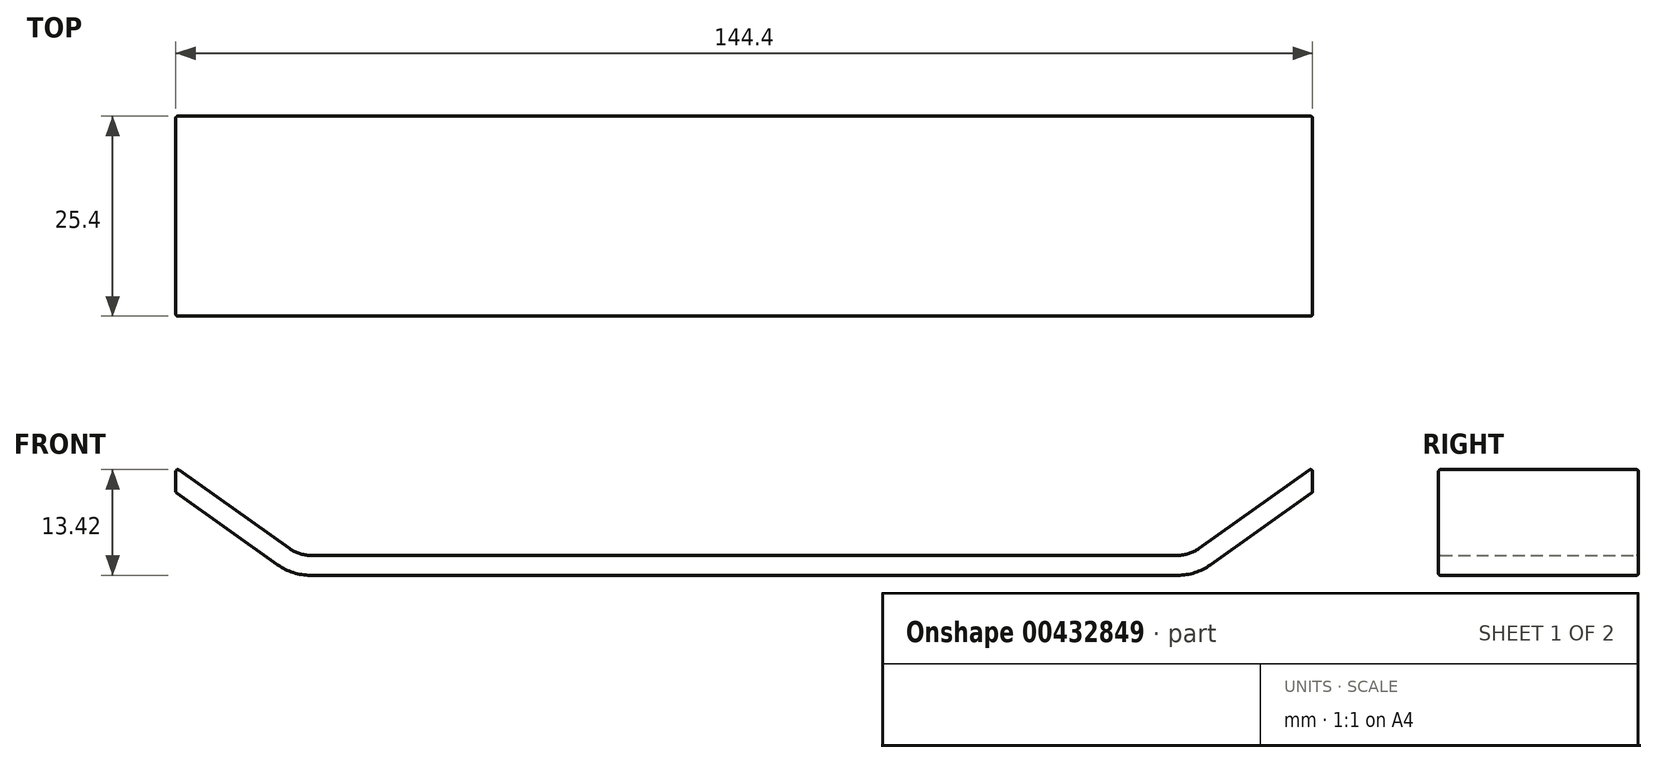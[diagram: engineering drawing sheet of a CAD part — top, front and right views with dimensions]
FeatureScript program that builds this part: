
annotation { "Feature Type Name" : "Feature", "Feature Type Description" : "" }
export const myFeature = defineFeature(function(context is Context, id is Id, definition is map)
    precondition{}
    {
        {
            var Q0;
            Q0=qCreatedBy(makeId("Front.planeOp"),FACE);
            var sketch = newSketch(context, id + "F0", { "sketchPlane" : qUnion([Q0])});
            skLineSegment(sketch, "E0", {"start": v(0, 0) * mm, "end": v(-55.08, 0) * mm});
            skArc(sketch, "E1", {"start": v(-59.23, 1.33) * mm, "mid": v(-57.26, 0.34) * mm, "end": v(-55.08, 0) * mm});
            skLineSegment(sketch, "E2", {"start": v(-59.23, 1.33) * mm, "end": v(-72.2, 10.54) * mm});
            skLineSegment(sketch, "E3.0", {"start": v(-57.76, 3.4) * mm, "end": v(-72.2, 13.66) * mm});
            skArc(sketch, "E3.1", {"start": v(-57.76, 3.4) * mm, "mid": v(-56.49, 2.76) * mm, "end": v(-55.08, 2.54) * mm});
            skLineSegment(sketch, "E3.2", {"start": v(0, 2.54) * mm, "end": v(-55.08, 2.54) * mm});
            skLineSegment(sketch, "E4", {"start": v(-72.2, 13.66) * mm, "end": v(-72.2, 10.54) * mm});
            skLineSegment(sketch, "E5.MirrorCS", {"start": v(72.2, 13.66) * mm, "end": v(72.2, 10.54) * mm});
            skArc(sketch, "E6.MirrorCS", {"start": v(57.76, 3.4) * mm, "mid": v(56.49, 2.76) * mm, "end": v(55.08, 2.54) * mm});
            skArc(sketch, "E7.MirrorCS", {"start": v(59.23, 1.33) * mm, "mid": v(57.26, 0.34) * mm, "end": v(55.08, 0) * mm});
            skLineSegment(sketch, "E8.MirrorCS", {"start": v(59.23, 1.33) * mm, "end": v(72.2, 10.54) * mm});
            skLineSegment(sketch, "E9.MirrorCS", {"start": v(0, 2.54) * mm, "end": v(55.08, 2.54) * mm});
            skLineSegment(sketch, "E10.MirrorCS", {"start": v(57.76, 3.4) * mm, "end": v(72.2, 13.66) * mm});
            skLineSegment(sketch, "E11.MirrorCS", {"start": v(0, 0) * mm, "end": v(55.08, 0) * mm});
            skSolve(sketch);
        }
        {
            var Q0;
            Q0=makeQuery(id+"F0.imprint","IMPRINT",FACE,{"disambiguationData":[TD([[makeQuery(id+"F0.imprint","IMPRINT",EDGE,{"derivedFrom":sQuery(id+"F0.wireOp",EDGE,"E0")}),-1.0]])]});
            extrude(context, id + "F1", {"entities" : qUnion([Q0]), "depth" : 25.4 * mm});
        }
        {
            var Q0;
            Q0=makeQuery(id+"F1.opExtrude","CAP_FACE",FACE,{"disambiguationData":[OSD([sQuery(id+"F0.wireOp",EDGE,"E0"),sQuery(id+"F0.wireOp",EDGE,"E1"),sQuery(id+"F0.wireOp",EDGE,"E2"),sQuery(id+"F0.wireOp",EDGE,"E3.0"),sQuery(id+"F0.wireOp",EDGE,"E3.1"),sQuery(id+"F0.wireOp",EDGE,"E3.2"),sQuery(id+"F0.wireOp",EDGE,"E4"),sQuery(id+"F0.wireOp",EDGE,"E5.MirrorCS"),sQuery(id+"F0.wireOp",EDGE,"E6.MirrorCS"),sQuery(id+"F0.wireOp",EDGE,"E7.MirrorCS"),sQuery(id+"F0.wireOp",EDGE,"E8.MirrorCS"),sQuery(id+"F0.wireOp",EDGE,"E9.MirrorCS"),sQuery(id+"F0.wireOp",EDGE,"E10.MirrorCS"),sQuery(id+"F0.wireOp",EDGE,"E11.MirrorCS")])],"isStart":true});
            var Q1;
            Q1=makeQuery(id+"F1.opExtrude","CAP_EDGE",EDGE,{"disambiguationData":[OSD([sQuery(id+"F0.wireOp",EDGE,"E3.0")])],"isStart":false});
            var Q2;
            Q2=makeQuery(id+"F1.opExtrude","CAP_EDGE",EDGE,{"disambiguationData":[OSD([sQuery(id+"F0.wireOp",EDGE,"E3.0")])],"isStart":true});
            var Q3;
            Q3=makeQuery(id+"F1.opExtrude","CAP_EDGE",EDGE,{"disambiguationData":[OSD([sQuery(id+"F0.wireOp",EDGE,"E3.2"),sQuery(id+"F0.wireOp",EDGE,"E9.MirrorCS")])],"isStart":false});
            var Q4;
            Q4=makeQuery(id+"F1.opExtrude","CAP_EDGE",EDGE,{"disambiguationData":[OSD([sQuery(id+"F0.wireOp",EDGE,"E2")])],"isStart":true});
            var Q5;
            Q5=makeQuery(id+"F1.opExtrude","SWEPT_EDGE",EDGE,{"disambiguationData":[OSD([sQuery(id+"F0.wireOp",EDGE,"E3.1"),sQuery(id+"F0.wireOp",EDGE,"E3.2")])]});
            var Q6;
            Q6=makeQuery(id+"F1.opExtrude","CAP_EDGE",EDGE,{"disambiguationData":[OSD([sQuery(id+"F0.wireOp",EDGE,"E5.MirrorCS")])],"isStart":true});
            var Q7;
            Q7=makeQuery(id+"F1.opExtrude","SWEPT_FACE",FACE,{"disambiguationData":[OSD([sQuery(id+"F0.wireOp",EDGE,"E4")])]});
            var Q8;
            Q8=makeQuery(id+"F1.opExtrude","SWEPT_FACE",FACE,{"disambiguationData":[OSD([sQuery(id+"F0.wireOp",EDGE,"E3.1")])]});
            var Q9;
            Q9=makeQuery(id+"F1.opExtrude","SWEPT_EDGE",EDGE,{"disambiguationData":[OSD([sQuery(id+"F0.wireOp",EDGE,"E3.0"),sQuery(id+"F0.wireOp",EDGE,"E4")])]});
            var Q10;
            Q10=makeQuery(id+"F1.opExtrude","SWEPT_EDGE",EDGE,{"disambiguationData":[OSD([sQuery(id+"F0.wireOp",EDGE,"E5.MirrorCS"),sQuery(id+"F0.wireOp",EDGE,"E10.MirrorCS")])]});
            var Q11;
            Q11=makeQuery(id+"F1.opExtrude","SWEPT_FACE",FACE,{"disambiguationData":[OSD([sQuery(id+"F0.wireOp",EDGE,"E10.MirrorCS")])]});
            var Q12;
            Q12=makeQuery(id+"F1.opExtrude","SWEPT_FACE",FACE,{"disambiguationData":[OSD([sQuery(id+"F0.wireOp",EDGE,"E5.MirrorCS")])]});
            var Q13;
            Q13=makeQuery(id+"F1.opExtrude","SWEPT_EDGE",EDGE,{"disambiguationData":[OSD([sQuery(id+"F0.wireOp",EDGE,"E3.0"),sQuery(id+"F0.wireOp",EDGE,"E3.1")])]});
            var Q14;
            Q14=makeQuery(id+"F1.opExtrude","SWEPT_FACE",FACE,{"disambiguationData":[OSD([sQuery(id+"F0.wireOp",EDGE,"E7.MirrorCS")])]});
            var Q15;
            Q15=makeQuery(id+"F1.opExtrude","SWEPT_EDGE",EDGE,{"disambiguationData":[OSD([sQuery(id+"F0.wireOp",EDGE,"E7.MirrorCS"),sQuery(id+"F0.wireOp",EDGE,"E8.MirrorCS")])]});
            var Q16;
            Q16=makeQuery(id+"F1.opExtrude","SWEPT_FACE",FACE,{"disambiguationData":[OSD([sQuery(id+"F0.wireOp",EDGE,"E2")])]});
            var Q17;
            Q17=makeQuery(id+"F1.opExtrude","SWEPT_FACE",FACE,{"disambiguationData":[OSD([sQuery(id+"F0.wireOp",EDGE,"E1")])]});
            var Q18;
            Q18=makeQuery(id+"F1.opExtrude","SWEPT_FACE",FACE,{"disambiguationData":[OSD([sQuery(id+"F0.wireOp",EDGE,"E0"),sQuery(id+"F0.wireOp",EDGE,"E11.MirrorCS")])]});
            var Q19;
            Q19=makeQuery(id+"F1.opExtrude","CAP_EDGE",EDGE,{"disambiguationData":[OSD([sQuery(id+"F0.wireOp",EDGE,"E5.MirrorCS")])],"isStart":false});
            var Q20;
            Q20=makeQuery(id+"F1.opExtrude","SWEPT_FACE",FACE,{"disambiguationData":[OSD([sQuery(id+"F0.wireOp",EDGE,"E3.0")])]});
            var Q21;
            Q21=makeQuery(id+"F1.opExtrude","SWEPT_FACE",FACE,{"disambiguationData":[OSD([sQuery(id+"F0.wireOp",EDGE,"E3.2"),sQuery(id+"F0.wireOp",EDGE,"E9.MirrorCS")])]});
            var Q22;
            Q22=makeQuery(id+"F1.opExtrude","SWEPT_FACE",FACE,{"disambiguationData":[OSD([sQuery(id+"F0.wireOp",EDGE,"E8.MirrorCS")])]});
            var Q23;
            Q23=makeQuery(id+"F1.opExtrude","SWEPT_EDGE",EDGE,{"disambiguationData":[OSD([sQuery(id+"F0.wireOp",EDGE,"E5.MirrorCS"),sQuery(id+"F0.wireOp",EDGE,"E8.MirrorCS")])]});
            var Q24;
            Q24=makeQuery(id+"F1.opExtrude","CAP_FACE",FACE,{"disambiguationData":[OSD([sQuery(id+"F0.wireOp",EDGE,"E0"),sQuery(id+"F0.wireOp",EDGE,"E1"),sQuery(id+"F0.wireOp",EDGE,"E2"),sQuery(id+"F0.wireOp",EDGE,"E3.0"),sQuery(id+"F0.wireOp",EDGE,"E3.1"),sQuery(id+"F0.wireOp",EDGE,"E3.2"),sQuery(id+"F0.wireOp",EDGE,"E4"),sQuery(id+"F0.wireOp",EDGE,"E5.MirrorCS"),sQuery(id+"F0.wireOp",EDGE,"E6.MirrorCS"),sQuery(id+"F0.wireOp",EDGE,"E7.MirrorCS"),sQuery(id+"F0.wireOp",EDGE,"E8.MirrorCS"),sQuery(id+"F0.wireOp",EDGE,"E9.MirrorCS"),sQuery(id+"F0.wireOp",EDGE,"E10.MirrorCS"),sQuery(id+"F0.wireOp",EDGE,"E11.MirrorCS")])],"isStart":false});
            var Q25;
            Q25=makeQuery(id+"F1.opExtrude","CAP_EDGE",EDGE,{"disambiguationData":[OSD([sQuery(id+"F0.wireOp",EDGE,"E7.MirrorCS")])],"isStart":true});
            var Q26;
            Q26=makeQuery(id+"F1.opExtrude","CAP_EDGE",EDGE,{"disambiguationData":[OSD([sQuery(id+"F0.wireOp",EDGE,"E2")])],"isStart":false});
            var Q27;
            Q27=makeQuery(id+"F1.opExtrude","CAP_EDGE",EDGE,{"disambiguationData":[OSD([sQuery(id+"F0.wireOp",EDGE,"E3.1")])],"isStart":true});
            var Q28;
            Q28=makeQuery(id+"F1.opExtrude","CAP_EDGE",EDGE,{"disambiguationData":[OSD([sQuery(id+"F0.wireOp",EDGE,"E10.MirrorCS")])],"isStart":false});
            var Q29;
            Q29=makeQuery(id+"F1.opExtrude","CAP_EDGE",EDGE,{"disambiguationData":[OSD([sQuery(id+"F0.wireOp",EDGE,"E8.MirrorCS")])],"isStart":false});
            var Q30;
            Q30=makeQuery(id+"F1.opExtrude","SWEPT_EDGE",EDGE,{"disambiguationData":[OSD([sQuery(id+"F0.wireOp",EDGE,"E6.MirrorCS"),sQuery(id+"F0.wireOp",EDGE,"E10.MirrorCS")])]});
            var Q31;
            Q31=makeQuery(id+"F1.opExtrude","CAP_EDGE",EDGE,{"disambiguationData":[OSD([sQuery(id+"F0.wireOp",EDGE,"E4")])],"isStart":false});
            var Q32;
            Q32=makeQuery(id+"F1.opExtrude","CAP_EDGE",EDGE,{"disambiguationData":[OSD([sQuery(id+"F0.wireOp",EDGE,"E3.1")])],"isStart":false});
            var Q33;
            Q33=makeQuery(id+"F1.opExtrude","CAP_EDGE",EDGE,{"disambiguationData":[OSD([sQuery(id+"F0.wireOp",EDGE,"E4")])],"isStart":true});
            var Q34;
            Q34=makeQuery(id+"F1.opExtrude","CAP_EDGE",EDGE,{"disambiguationData":[OSD([sQuery(id+"F0.wireOp",EDGE,"E7.MirrorCS")])],"isStart":false});
            var Q35;
            Q35=makeQuery(id+"F1.opExtrude","CAP_EDGE",EDGE,{"disambiguationData":[OSD([sQuery(id+"F0.wireOp",EDGE,"E10.MirrorCS")])],"isStart":true});
            var Q36;
            Q36=makeQuery(id+"F1.opExtrude","SWEPT_FACE",FACE,{"disambiguationData":[OSD([sQuery(id+"F0.wireOp",EDGE,"E6.MirrorCS")])]});
            var Q37;
            Q37=makeQuery(id+"F1.opExtrude","CAP_EDGE",EDGE,{"disambiguationData":[OSD([sQuery(id+"F0.wireOp",EDGE,"E0"),sQuery(id+"F0.wireOp",EDGE,"E11.MirrorCS")])],"isStart":true});
            var Q38;
            Q38=makeQuery(id+"F1.opExtrude","SWEPT_EDGE",EDGE,{"disambiguationData":[OSD([sQuery(id+"F0.wireOp",EDGE,"E7.MirrorCS"),sQuery(id+"F0.wireOp",EDGE,"E11.MirrorCS")])]});
            var Q39;
            Q39=makeQuery(id+"F1.opExtrude","SWEPT_EDGE",EDGE,{"disambiguationData":[OSD([sQuery(id+"F0.wireOp",EDGE,"E2"),sQuery(id+"F0.wireOp",EDGE,"E4")])]});
            var Q40;
            Q40=makeQuery(id+"F1.opExtrude","SWEPT_EDGE",EDGE,{"disambiguationData":[OSD([sQuery(id+"F0.wireOp",EDGE,"E1"),sQuery(id+"F0.wireOp",EDGE,"E2")])]});
            var Q41;
            Q41=makeQuery(id+"F1.opExtrude","SWEPT_EDGE",EDGE,{"disambiguationData":[OSD([sQuery(id+"F0.wireOp",EDGE,"E0"),sQuery(id+"F0.wireOp",EDGE,"E1")])]});
            var Q42;
            Q42=makeQuery(id+"F1.opExtrude","CAP_EDGE",EDGE,{"disambiguationData":[OSD([sQuery(id+"F0.wireOp",EDGE,"E1")])],"isStart":false});
            var Q43;
            Q43=makeQuery(id+"F1.opExtrude","CAP_EDGE",EDGE,{"disambiguationData":[OSD([sQuery(id+"F0.wireOp",EDGE,"E1")])],"isStart":true});
            var Q44;
            Q44=makeQuery(id+"F1.opExtrude","CAP_EDGE",EDGE,{"disambiguationData":[OSD([sQuery(id+"F0.wireOp",EDGE,"E0"),sQuery(id+"F0.wireOp",EDGE,"E11.MirrorCS")])],"isStart":false});
            var Q45;
            Q45=makeQuery(id+"F1.opExtrude","CAP_EDGE",EDGE,{"disambiguationData":[OSD([sQuery(id+"F0.wireOp",EDGE,"E8.MirrorCS")])],"isStart":true});
            var Q46;
            Q46=makeQuery(id+"F1.opExtrude","CAP_EDGE",EDGE,{"disambiguationData":[OSD([sQuery(id+"F0.wireOp",EDGE,"E3.2"),sQuery(id+"F0.wireOp",EDGE,"E9.MirrorCS")])],"isStart":true});
            var Q47;
            Q47=makeQuery(id+"F1.opExtrude","CAP_EDGE",EDGE,{"disambiguationData":[OSD([sQuery(id+"F0.wireOp",EDGE,"E6.MirrorCS")])],"isStart":false});
            var Q48;
            Q48=makeQuery(id+"F1.opExtrude","CAP_EDGE",EDGE,{"disambiguationData":[OSD([sQuery(id+"F0.wireOp",EDGE,"E6.MirrorCS")])],"isStart":true});
            var Q49;
            Q49=makeQuery(id+"F1.opExtrude","SWEPT_EDGE",EDGE,{"disambiguationData":[OSD([sQuery(id+"F0.wireOp",EDGE,"E6.MirrorCS"),sQuery(id+"F0.wireOp",EDGE,"E9.MirrorCS")])]});
            fillet(context, id + "F2", {"entities" : qUnion([Q0, Q1, Q2, Q3, Q4, Q5, Q6, Q7, Q8, Q9, Q10, Q11, Q12, Q13, Q14, Q15, Q16, Q17, Q18, Q19, Q20, Q21, Q22, Q23, Q24, Q25, Q26, Q27, Q28, Q29, Q30, Q31, Q32, Q33, Q34, Q35, Q36, Q37, Q38, Q39, Q40, Q41, Q42, Q43, Q44, Q45, Q46, Q47, Q48, Q49]), "radius" : 0.25 * mm, "tangentPropagation" : true, "allowEdgeOverflow" : false});
        }
    });
